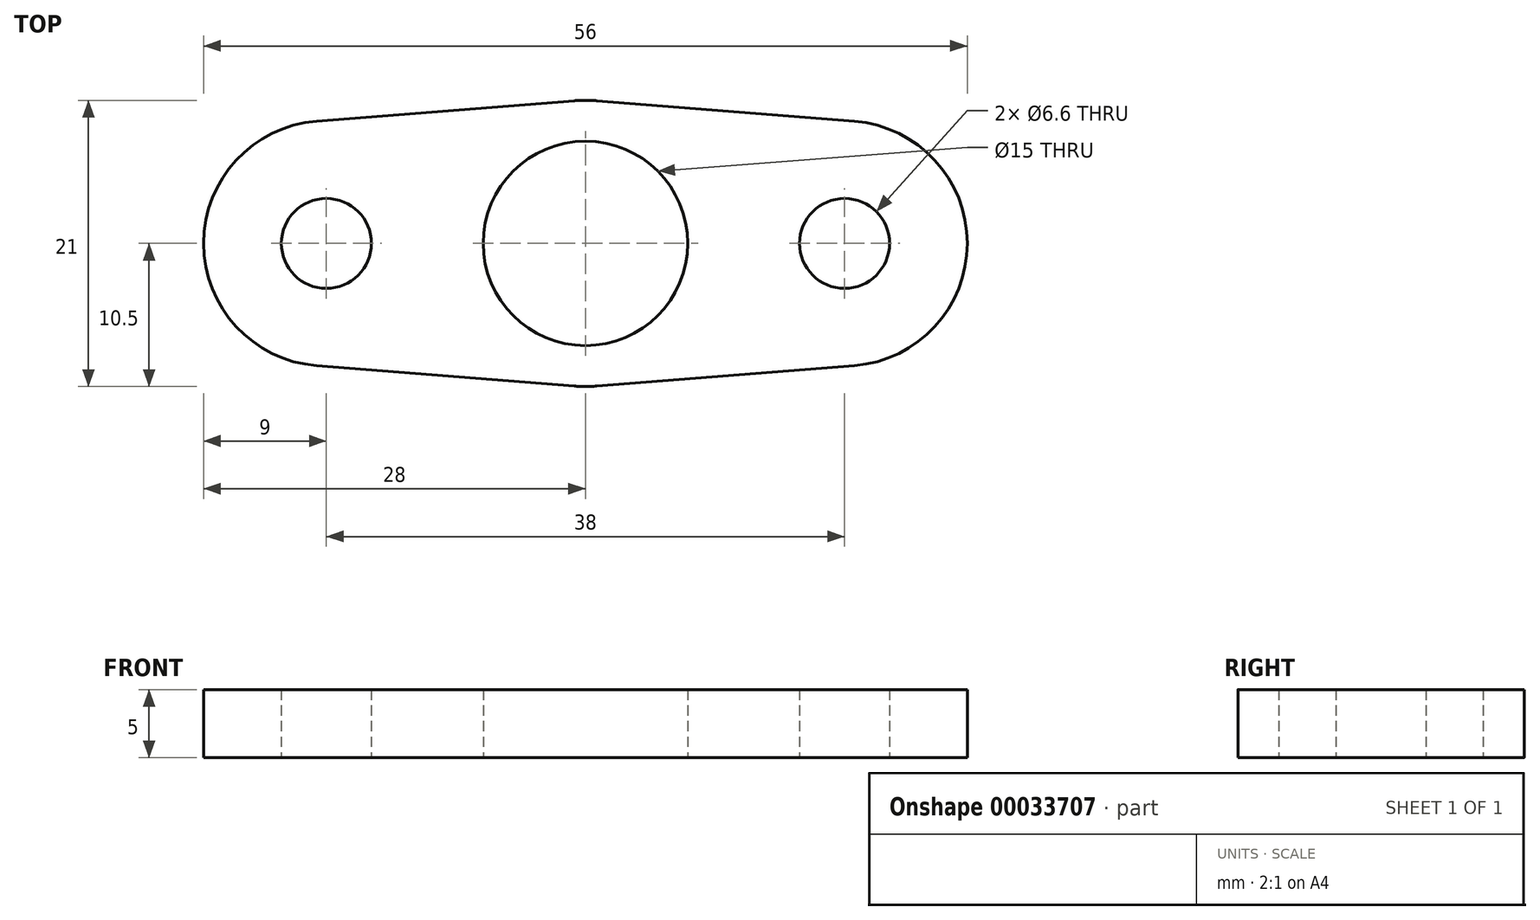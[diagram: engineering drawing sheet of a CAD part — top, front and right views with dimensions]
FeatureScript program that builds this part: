
annotation { "Feature Type Name" : "Feature", "Feature Type Description" : "" }
export const myFeature = defineFeature(function(context is Context, id is Id, definition is map)
    precondition{}
    {
        {
            var Q0;
            Q0=qCreatedBy(makeId("Top.planeOp"),FACE);
            var sketch = newSketch(context, id + "F0", { "sketchPlane" : qUnion([Q0])});
            skCircle(sketch, "E0", {"center": v(-19, 0) * mm, "radius": 3.3 * mm});
            skCircle(sketch, "E1", {"center": v(19, 0) * mm, "radius": 3.3 * mm});
            skCircle(sketch, "E2", {"center": v(0, 0) * mm, "radius": 19 * mm, "construction": true});
            skArc(sketch, "E3", {"start": v(-19.71, 8.97) * mm, "mid": v(-28, 0) * mm, "end": v(-19.71, -8.97) * mm});
            skArc(sketch, "E4", {"start": v(19.71, -8.97) * mm, "mid": v(28, 0) * mm, "end": v(19.71, 8.97) * mm});
            skLineSegment(sketch, "E5", {"start": v(-19.71, 8.97) * mm, "end": v(-0.83, 10.47) * mm});
            skLineSegment(sketch, "E6", {"start": v(-19.71, -8.97) * mm, "end": v(-0.83, -10.47) * mm});
            skCircle(sketch, "E7", {"center": v(0, 0) * mm, "radius": 7.5 * mm});
            skArc(sketch, "E8", {"start": v(0.83, 10.47) * mm, "mid": v(0, 10.5) * mm, "end": v(-0.83, 10.47) * mm});
            skLineSegment(sketch, "E9.trimOffspring", {"start": v(0.83, 10.47) * mm, "end": v(19.71, 8.97) * mm});
            skLineSegment(sketch, "E10.trimOffspring", {"start": v(0.83, -10.47) * mm, "end": v(19.71, -8.97) * mm});
            skArc(sketch, "E11.trimOffspring", {"start": v(-0.83, -10.47) * mm, "mid": v(0, -10.5) * mm, "end": v(0.83, -10.47) * mm});
            skSolve(sketch);
        }
        {
            var Q0;
            Q0 = qSketchRegion(id + "F0", true);
            extrude(context, id + "F1", {"entities" : qUnion([Q0]), "depth" : 5 * mm});
        }
    });
